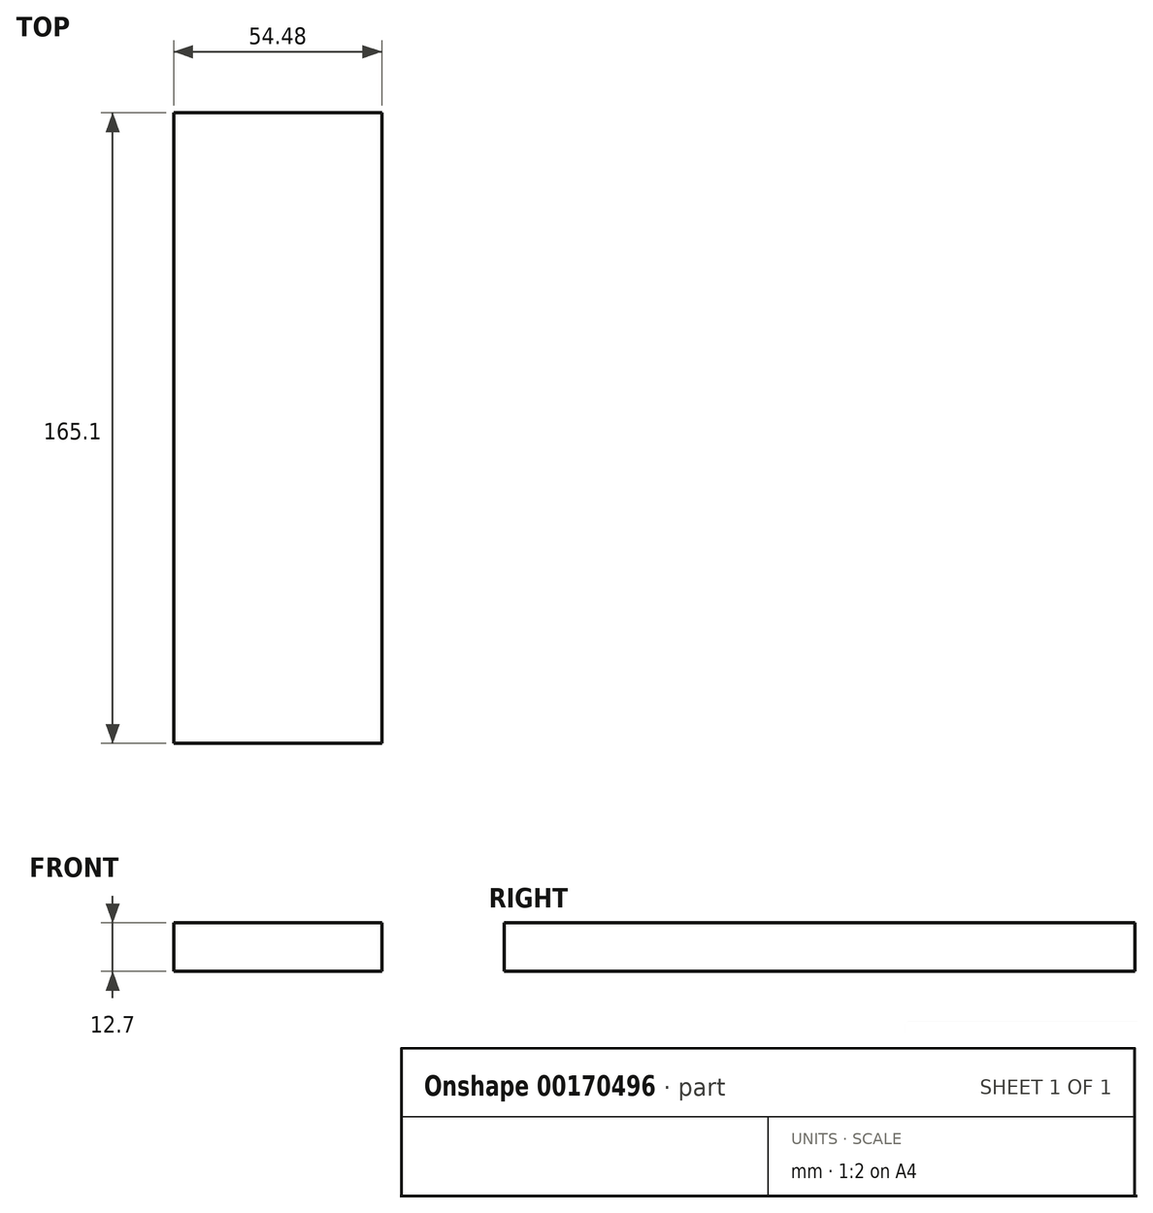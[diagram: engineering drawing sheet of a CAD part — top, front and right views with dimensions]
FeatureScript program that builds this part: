
annotation { "Feature Type Name" : "Feature", "Feature Type Description" : "" }
export const myFeature = defineFeature(function(context is Context, id is Id, definition is map)
    precondition{}
    {
        {
            var Q0;
            Q0=qCreatedBy(makeId("Top.planeOp"),FACE);
            var sketch = newSketch(context, id + "F0", { "sketchPlane" : qUnion([Q0])});
            skLineSegment(sketch, "E0.bottom", {"start": v(-31.66, 103.38) * mm, "end": v(22.82, 103.38) * mm});
            skLineSegment(sketch, "E0.top", {"start": v(-31.66, -61.72) * mm, "end": v(22.82, -61.72) * mm});
            skLineSegment(sketch, "E0.left", {"start": v(-31.66, 103.38) * mm, "end": v(-31.66, -61.72) * mm});
            skLineSegment(sketch, "E0.right", {"start": v(22.82, 103.38) * mm, "end": v(22.82, -61.72) * mm});
            skSolve(sketch);
        }
        {
            var Q0;
            Q0=makeQuery(id+"F0.imprint","IMPRINT",FACE,{"disambiguationData":[TD([[makeQuery(id+"F0.imprint","IMPRINT",EDGE,{"derivedFrom":sQuery(id+"F0.wireOp",EDGE,"E0.bottom")}),-1.0]])]});
            extrude(context, id + "F1", {"entities" : qUnion([Q0]), "depth" : 12.7 * mm});
        }
    });
